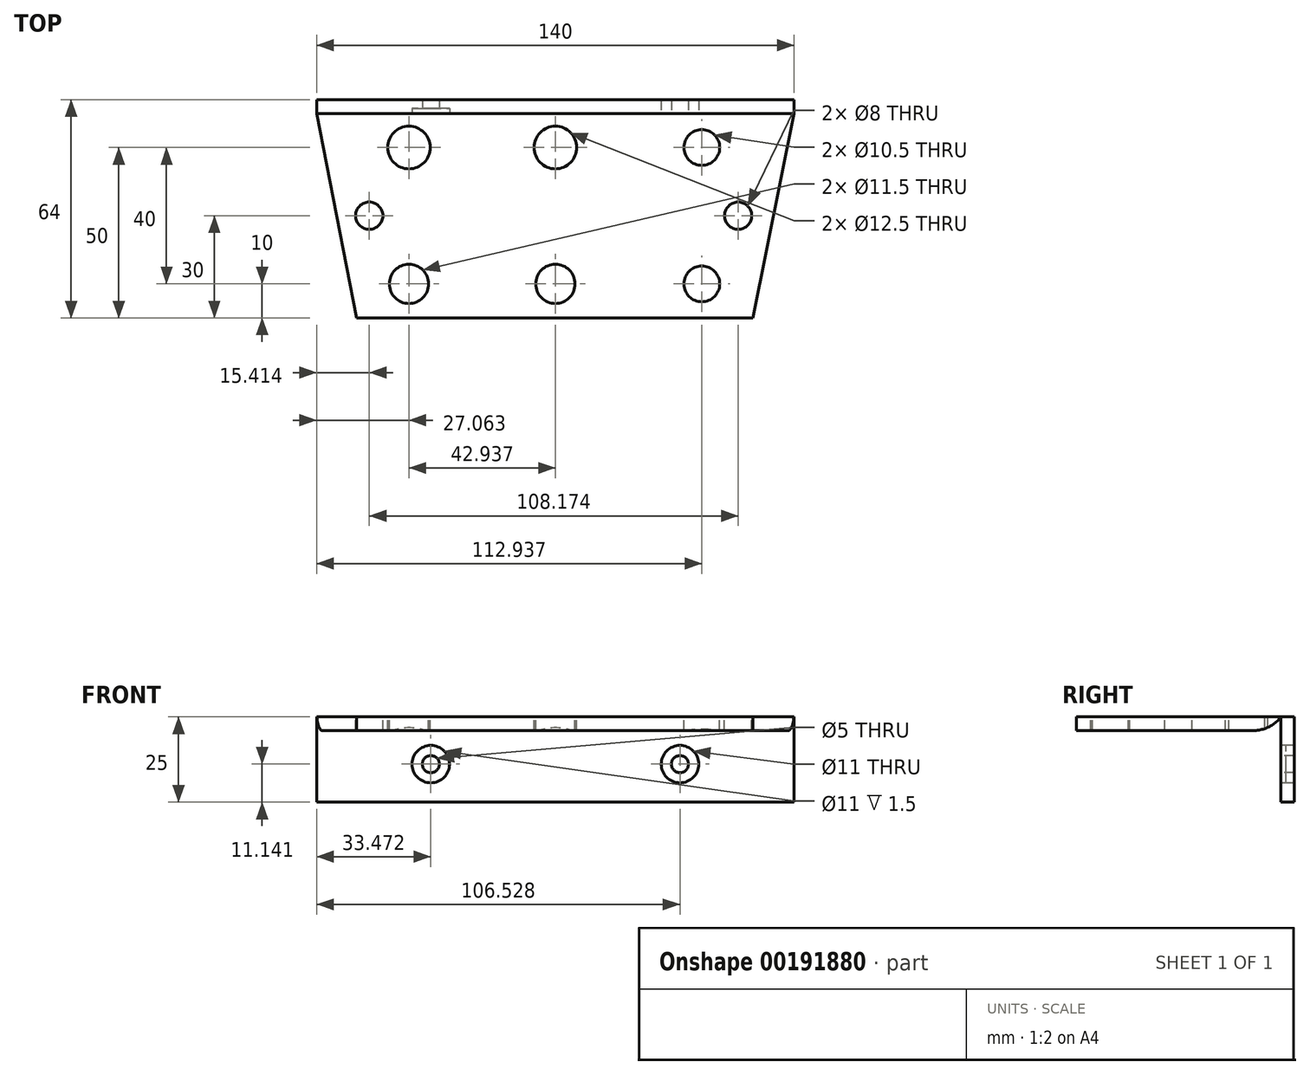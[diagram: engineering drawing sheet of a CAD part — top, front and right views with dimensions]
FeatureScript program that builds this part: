
annotation { "Feature Type Name" : "Feature", "Feature Type Description" : "" }
export const myFeature = defineFeature(function(context is Context, id is Id, definition is map)
    precondition{}
    {
        {
            var Q0;
            Q0=qCreatedBy(makeId("Top.planeOp"),FACE);
            var sketch = newSketch(context, id + "F0", { "sketchPlane" : qUnion([Q0])});
            skLineSegment(sketch, "E0.bottom", {"start": v(57.94, -30) * mm, "end": v(-58.25, -30) * mm});
            skLineSegment(sketch, "E0.top", {"start": v(57.94, 30) * mm, "end": v(-58.25, 30) * mm});
            skPoint(sketch, "E0.middle", {"position": v(0, 0) * mm});
            skLineSegment(sketch, "E1", {"start": v(-70, 20) * mm, "end": v(-68.04, 20) * mm, "construction": true});
            skLineSegment(sketch, "E2", {"start": v(0, 30) * mm, "end": v(0, 13.75) * mm, "construction": true});
            skCircle(sketch, "E3", {"center": v(0, 20) * mm, "radius": 6.25 * mm});
            skCircle(sketch, "E4", {"center": v(0, -20) * mm, "radius": 5.75 * mm});
            skLineSegment(sketch, "E5", {"start": v(-42.94, 30) * mm, "end": v(-42.94, 13.75) * mm});
            skCircle(sketch, "E6", {"center": v(-42.94, 20) * mm, "radius": 6.25 * mm});
            skCircle(sketch, "E7", {"center": v(-42.94, -20) * mm, "radius": 5.75 * mm});
            skCircle(sketch, "E8", {"center": v(42.94, 20) * mm, "radius": 5.25 * mm});
            skCircle(sketch, "E9", {"center": v(42.94, -20) * mm, "radius": 5.25 * mm});
            skPoint(sketch, "E10.orphan", {"position": v(-70, 30) * mm});
            skPoint(sketch, "E11.orphan", {"position": v(-70, -30) * mm});
            skPoint(sketch, "E12.orphan", {"position": v(70, 0) * mm});
            skPoint(sketch, "E13.orphan", {"position": v(70, 20) * mm});
            skPoint(sketch, "E14.orphan", {"position": v(70, 30) * mm});
            skPoint(sketch, "E15.orphan", {"position": v(70, -30) * mm});
            skLineSegment(sketch, "E16.trimOffspring", {"start": v(49.59, 0) * mm, "end": v(57.59, 0) * mm, "construction": true});
            skLineSegment(sketch, "E17", {"start": v(-58.25, -30) * mm, "end": v(-70, 30) * mm});
            skLineSegment(sketch, "E18", {"start": v(-70, 30) * mm, "end": v(70, 30) * mm});
            skLineSegment(sketch, "E19", {"start": v(57.94, -30) * mm, "end": v(70, 30) * mm});
            skCircle(sketch, "E20", {"center": v(53.59, 0) * mm, "radius": 4 * mm});
            skCircle(sketch, "E21", {"center": v(-54.59, 0) * mm, "radius": 4 * mm});
            skPoint(sketch, "E22.orphan", {"position": v(42.94, 30) * mm});
            skPoint(sketch, "E23.trimOffspring.end.orphan", {"position": v(42.94, -30) * mm});
            skLineSegment(sketch, "E24.trimOffspring", {"start": v(-42.94, -14.25) * mm, "end": v(-42.94, -30) * mm});
            skPoint(sketch, "E25.start.orphan", {"position": v(-42.94, 0) * mm});
            skLineSegment(sketch, "E26.trimOffspring", {"start": v(0, -14.25) * mm, "end": v(0, -30) * mm, "construction": true});
            skLineSegment(sketch, "E27.trimOffspring", {"start": v(6.25, 20) * mm, "end": v(48.19, 20) * mm, "construction": true});
            skLineSegment(sketch, "E28.trimOffspring", {"start": v(-5.75, -20) * mm, "end": v(5.75, -20) * mm, "construction": true});
            skLineSegment(sketch, "E29.trimOffspring", {"start": v(37.69, -20) * mm, "end": v(48.19, -20) * mm, "construction": true});
            skLineSegment(sketch, "E30.top", {"start": v(-70, 34) * mm, "end": v(70, 34) * mm});
            skLineSegment(sketch, "E30.left", {"start": v(-70, 30) * mm, "end": v(-70, 34) * mm});
            skLineSegment(sketch, "E30.right", {"start": v(70, 30) * mm, "end": v(70, 34) * mm});
            skSolve(sketch);
        }
        {
            var Q0;
            Q0=makeQuery(id+"F0.imprint","IMPRINT",FACE,{"disambiguationData":[TD([[makeQuery(id+"F0.imprint","IMPRINT",EDGE,{"derivedFrom":sQuery(id+"F0.wireOp",EDGE,"E3")}),-1.0]])]});
            extrude(context, id + "F1", {"entities" : qUnion([Q0]), "oppositeDirection" : true, "depth" : 4 * mm});
        }
        {
            var Q0;
            Q0=makeQuery(id+"F0.imprint","IMPRINT",FACE,{"disambiguationData":[TD([[makeQuery(id+"F0.imprint","IMPRINT",EDGE,{"derivedFrom":sQuery(id+"F0.wireOp",EDGE,"E30.top")}),-1.0]])]});
            extrude(context, id + "F2", {"entities" : qUnion([Q0]), "oppositeDirection" : true, "depth" : 25 * mm});
        }
        {
            var Q0;
            Q0=makeQuery(id+"F2.opExtrude","SWEPT_FACE",FACE,{"disambiguationData":[OSD([sQuery(id+"F0.wireOp",EDGE,"E18")])]});
            var sketch = newSketch(context, id + "F3", { "sketchPlane" : qUnion([Q0])});
            skLineSegment(sketch, "E31.bottom", {"start": v(-70, -25) * mm, "end": v(70, -25) * mm});
            skLineSegment(sketch, "E31.top", {"start": v(-70, -25) * mm, "end": v(70, -25) * mm});
            skLineSegment(sketch, "E31.left", {"start": v(-70, -25) * mm, "end": v(-70, -25) * mm});
            skLineSegment(sketch, "E31.right", {"start": v(70, -25) * mm, "end": v(70, -25) * mm});
            skLineSegment(sketch, "E32.top", {"start": v(-70, -4.2) * mm, "end": v(70, -4.2) * mm});
            skLineSegment(sketch, "E32.left", {"start": v(-70, -25) * mm, "end": v(-70, -4.2) * mm});
            skLineSegment(sketch, "E32.right", {"start": v(70, -25) * mm, "end": v(70, -4.2) * mm});
            skSolve(sketch);
        }
        {
            var Q0;
            Q0=makeQuery(id+"F3.imprint","IMPRINT",FACE,{"disambiguationData":[TD([[makeQuery(id+"F3.imprint","IMPRINT",EDGE,{"derivedFrom":sQuery(id+"F3.wireOp",EDGE,"E31.bottom")}),1.0]])]});
            var sketch = newSketch(context, id + "F4", { "sketchPlane" : qUnion([Q0])});
            skCircle(sketch, "E33", {"center": v(-36.53, -13.86) * mm, "radius": 2.5 * mm});
            skLineSegment(sketch, "E34", {"start": v(0, -25.03) * mm, "end": v(0, 0) * mm, "construction": true});
            skCircle(sketch, "E35", {"center": v(-36.53, -13.86) * mm, "radius": 5.5 * mm});
            skCircle(sketch, "E36.MirrorC", {"center": v(36.53, -13.86) * mm, "radius": 5.5 * mm});
            skCircle(sketch, "E37.MirrorC", {"center": v(36.53, -13.86) * mm, "radius": 2.5 * mm});
            skSolve(sketch);
        }
        {
            var Q0;
            Q0=makeQuery(id+"F4.imprint","IMPRINT",FACE,{"disambiguationData":[TD([[makeQuery(id+"F4.imprint","IMPRINT",EDGE,{"derivedFrom":sQuery(id+"F4.wireOp",EDGE,"E33")}),1.0]])]});
            var Q1;
            Q1=makeQuery(id+"F4.imprint","IMPRINT",FACE,{"disambiguationData":[TD([[makeQuery(id+"F4.imprint","IMPRINT",EDGE,{"derivedFrom":sQuery(id+"F4.wireOp",EDGE,"E37.MirrorC")}),-1.0]])]});
            extrude(context, id + "F5", {"entities" : qUnion([Q0, Q1]), "operationType" : NewBodyOperationType.REMOVE, "oppositeDirection" : true, "depth" : 25 * mm});
        }
        {
            var Q0;
            Q0 = qSketchRegion(id + "F4", true);
            extrude(context, id + "F6", {"entities" : qUnion([Q0]), "operationType" : NewBodyOperationType.REMOVE, "oppositeDirection" : true, "depth" : 1.5 * mm});
        }
        {
            var Q0;
            Q0=makeQuery(id+"F1.opExtrude","CAP_EDGE",EDGE,{"disambiguationData":[OSD([sQuery(id+"F0.wireOp",EDGE,"E18")])],"isStart":false});
            fillet(context, id + "F7", {"entities" : qUnion([Q0]), "radius" : 10 * mm, "tangentPropagation" : true, "allowEdgeOverflow" : false});
        }
    });
